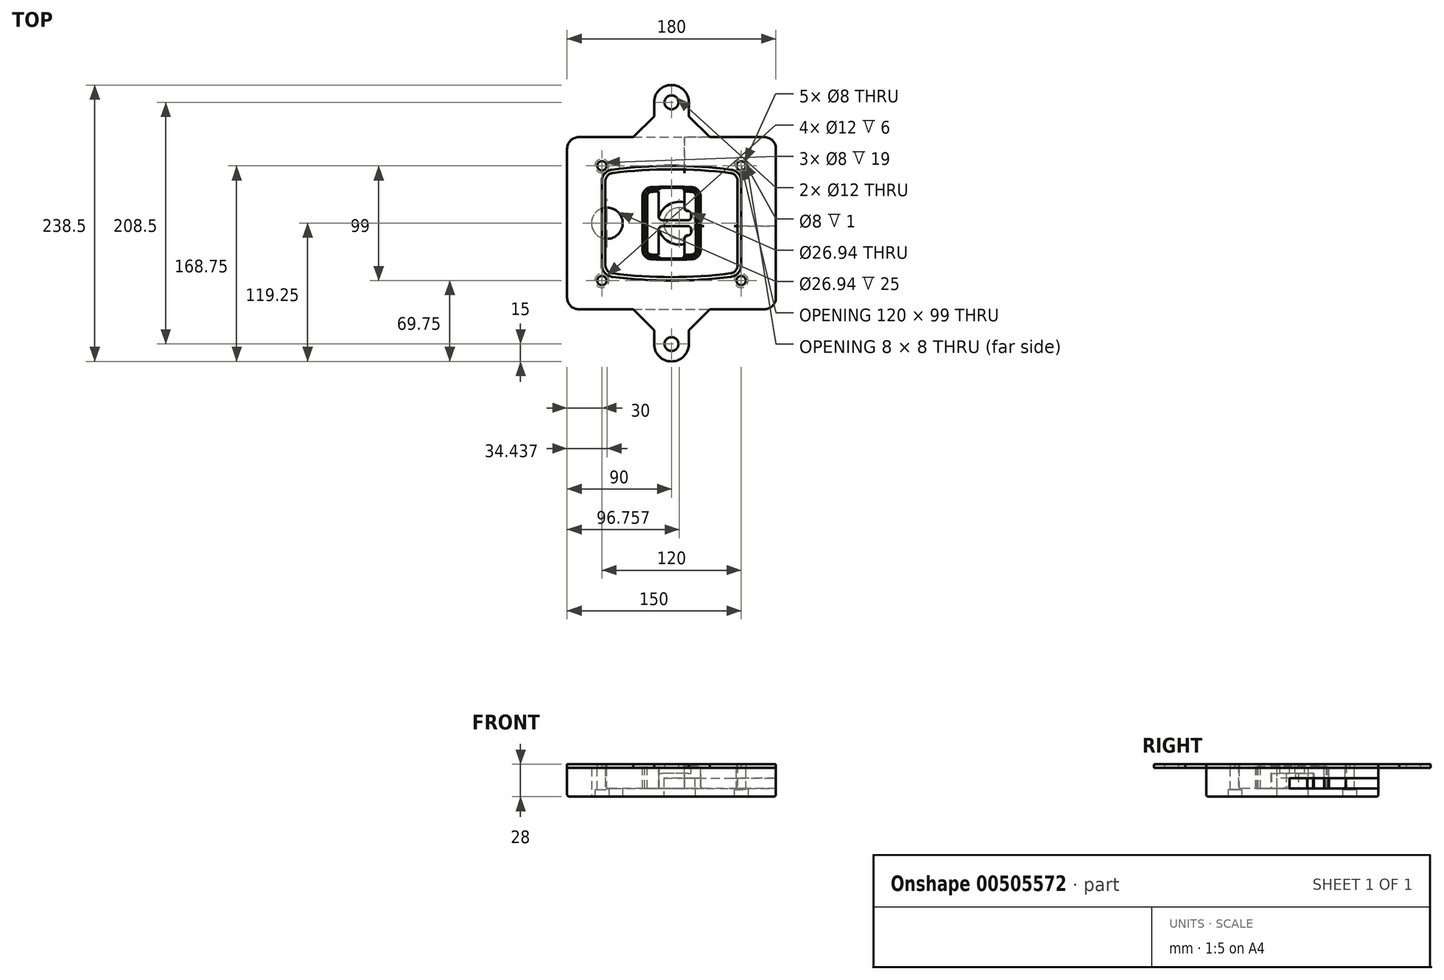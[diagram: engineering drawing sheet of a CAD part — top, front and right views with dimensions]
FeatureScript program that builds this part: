
annotation { "Feature Type Name" : "Feature", "Feature Type Description" : "" }
export const myFeature = defineFeature(function(context is Context, id is Id, definition is map)
    precondition{}
    {
        {
            var Q0;
            Q0=qCreatedBy(makeId("Top.planeOp"),FACE);
            var sketch = newSketch(context, id + "F0", { "sketchPlane" : qUnion([Q0])});
            skPoint(sketch, "E0.rect.middle", {"position": v(0, 0) * mm});
            skLineSegment(sketch, "E1.bottom", {"start": v(-80, -74.25) * mm, "end": v(80, -74.25) * mm});
            skLineSegment(sketch, "E1.top", {"start": v(-80, 74.25) * mm, "end": v(80, 74.25) * mm});
            skLineSegment(sketch, "E1.left", {"start": v(-90, -64.25) * mm, "end": v(-90, 64.25) * mm});
            skLineSegment(sketch, "E1.right", {"start": v(90, -64.25) * mm, "end": v(90, 64.25) * mm});
            skLineSegment(sketch, "E2", {"start": v(-90, 74.25) * mm, "end": v(90, -74.25) * mm, "construction": true});
            skLineSegment(sketch, "E3", {"start": v(90, 74.25) * mm, "end": v(-90, -74.25) * mm, "construction": true});
            skCircle(sketch, "E4", {"center": v(-60, 49.5) * mm, "radius": 4 * mm});
            skCircle(sketch, "E5", {"center": v(60, 49.5) * mm, "radius": 4 * mm});
            skCircle(sketch, "E6", {"center": v(60, -49.5) * mm, "radius": 4 * mm});
            skCircle(sketch, "E7", {"center": v(-60, -49.5) * mm, "radius": 4 * mm});
            skLineSegment(sketch, "E8", {"start": v(-60, 49.5) * mm, "end": v(60, 49.5) * mm, "construction": true});
            skLineSegment(sketch, "E9", {"start": v(60, 49.5) * mm, "end": v(60, -49.5) * mm, "construction": true});
            skLineSegment(sketch, "E10", {"start": v(60, -49.5) * mm, "end": v(-60, -49.5) * mm, "construction": true});
            skLineSegment(sketch, "E11", {"start": v(-60, -49.5) * mm, "end": v(-60, 49.5) * mm, "construction": true});
            skLineSegment(sketch, "E12", {"start": v(-60, 36.3) * mm, "end": v(-60, -36.3) * mm});
            skLineSegment(sketch, "E13", {"start": v(60, 36.3) * mm, "end": v(60, -36.3) * mm});
            skArc(sketch, "E14", {"start": v(51.27, 46.22) * mm, "mid": v(0, 49.5) * mm, "end": v(-51.27, 46.22) * mm});
            skArc(sketch, "E15", {"start": v(-51.27, -46.22) * mm, "mid": v(0, -49.5) * mm, "end": v(51.27, -46.22) * mm});
            skLineSegment(sketch, "E16", {"start": v(-60, 0) * mm, "end": v(60, 0) * mm, "construction": true});
            skPoint(sketch, "E17.visualSharp", {"position": v(-60, -45) * mm});
            skArc(sketch, "E17.filletArc", {"start": v(-60, -36.3) * mm, "mid": v(-57.5, -42.9) * mm, "end": v(-51.27, -46.22) * mm});
            skPoint(sketch, "E18.visualSharp", {"position": v(-60, 45) * mm});
            skArc(sketch, "E18.filletArc", {"start": v(-51.27, 46.22) * mm, "mid": v(-57.5, 42.9) * mm, "end": v(-60, 36.3) * mm});
            skPoint(sketch, "E19.visualSharp", {"position": v(60, 45) * mm});
            skArc(sketch, "E19.filletArc", {"start": v(60, 36.3) * mm, "mid": v(57.5, 42.9) * mm, "end": v(51.27, 46.22) * mm});
            skPoint(sketch, "E20.visualSharp", {"position": v(60, -45) * mm});
            skArc(sketch, "E20.filletArc", {"start": v(51.27, -46.22) * mm, "mid": v(57.5, -42.9) * mm, "end": v(60, -36.3) * mm});
            skPoint(sketch, "E21.visualSharp", {"position": v(-90, 74.25) * mm});
            skArc(sketch, "E21.filletArc", {"start": v(-80, 74.25) * mm, "mid": v(-87.07, 71.32) * mm, "end": v(-90, 64.25) * mm});
            skPoint(sketch, "E22.visualSharp", {"position": v(90, 74.25) * mm});
            skArc(sketch, "E22.filletArc", {"start": v(90, 64.25) * mm, "mid": v(87.07, 71.32) * mm, "end": v(80, 74.25) * mm});
            skPoint(sketch, "E23.visualSharp", {"position": v(90, -74.25) * mm});
            skArc(sketch, "E23.filletArc", {"start": v(80, -74.25) * mm, "mid": v(87.07, -71.32) * mm, "end": v(90, -64.25) * mm});
            skPoint(sketch, "E24.visualSharp", {"position": v(-90, -74.25) * mm});
            skArc(sketch, "E24.filletArc", {"start": v(-90, -64.25) * mm, "mid": v(-87.07, -71.32) * mm, "end": v(-80, -74.25) * mm});
            skArc(sketch, "E25.0", {"start": v(57, 36.3) * mm, "mid": v(55.26, 40.92) * mm, "end": v(50.9, 43.24) * mm});
            skLineSegment(sketch, "E25.1", {"start": v(57, 36.3) * mm, "end": v(57, -36.3) * mm});
            skArc(sketch, "E25.2", {"start": v(50.9, -43.24) * mm, "mid": v(55.26, -40.92) * mm, "end": v(57, -36.3) * mm});
            skArc(sketch, "E25.3", {"start": v(-50.9, -43.24) * mm, "mid": v(0, -46.5) * mm, "end": v(50.9, -43.24) * mm});
            skArc(sketch, "E25.4", {"start": v(-57, -36.3) * mm, "mid": v(-55.26, -40.92) * mm, "end": v(-50.9, -43.24) * mm});
            skArc(sketch, "E25.5", {"start": v(50.9, 43.24) * mm, "mid": v(0, 46.5) * mm, "end": v(-50.9, 43.24) * mm});
            skLineSegment(sketch, "E25.6", {"start": v(-57, 36.3) * mm, "end": v(-57, -36.3) * mm});
            skArc(sketch, "E25.7", {"start": v(-50.9, 43.24) * mm, "mid": v(-55.26, 40.92) * mm, "end": v(-57, 36.3) * mm});
            skArc(sketch, "E26.0", {"start": v(-51.78, 50.19) * mm, "mid": v(-60.51, 45.55) * mm, "end": v(-64, 36.3) * mm});
            skArc(sketch, "E26.1", {"start": v(51.78, 50.19) * mm, "mid": v(0, 53.5) * mm, "end": v(-51.78, 50.19) * mm});
            skArc(sketch, "E26.2", {"start": v(64, 36.3) * mm, "mid": v(60.51, 45.55) * mm, "end": v(51.78, 50.19) * mm});
            skLineSegment(sketch, "E26.3", {"start": v(64, 36.3) * mm, "end": v(64, -36.3) * mm});
            skArc(sketch, "E26.4", {"start": v(51.78, -50.19) * mm, "mid": v(60.51, -45.55) * mm, "end": v(64, -36.3) * mm});
            skLineSegment(sketch, "E26.5", {"start": v(-64, 36.3) * mm, "end": v(-64, -36.3) * mm});
            skArc(sketch, "E26.6", {"start": v(-51.78, -50.19) * mm, "mid": v(0, -53.5) * mm, "end": v(51.78, -50.19) * mm});
            skArc(sketch, "E26.7", {"start": v(-64, -36.3) * mm, "mid": v(-60.51, -45.55) * mm, "end": v(-51.78, -50.19) * mm});
            skSolve(sketch);
        }
        {
            var Q0;
            Q0=makeQuery(id+"F0.imprint","IMPRINT",FACE,{"disambiguationData":[TD([[makeQuery(id+"F0.imprint","IMPRINT",EDGE,{"derivedFrom":sQuery(id+"F0.wireOp",EDGE,"E1.bottom")}),1.0]])]});
            var Q1;
            Q1=makeQuery(id+"F0.imprint","IMPRINT",FACE,{"disambiguationData":[TD([[makeQuery(id+"F0.imprint","IMPRINT",EDGE,{"derivedFrom":sQuery(id+"F0.wireOp",EDGE,"E12")}),1.0]])]});
            var Q2;
            Q2=makeQuery(id+"F0.imprint","IMPRINT",FACE,{"disambiguationData":[TD([[makeQuery(id+"F0.imprint","IMPRINT",EDGE,{"derivedFrom":sQuery(id+"F0.wireOp",EDGE,"E25.0")}),1.0]])]});
            var Q3;
            Q3=makeQuery(id+"F0.imprint","IMPRINT",FACE,{"disambiguationData":[TD([[makeQuery(id+"F0.imprint","IMPRINT",EDGE,{"derivedFrom":sQuery(id+"F0.wireOp",EDGE,"E12")}),-1.0]])]});
            extrude(context, id + "F1", {"entities" : qUnion([Q0, Q1, Q2, Q3]), "oppositeDirection" : true, "depth" : 25 * mm});
        }
        {
            var Q0;
            Q0=makeQuery(id+"F0.imprint","IMPRINT",FACE,{"disambiguationData":[TD([[makeQuery(id+"F0.imprint","IMPRINT",EDGE,{"derivedFrom":sQuery(id+"F0.wireOp",EDGE,"E12")}),1.0]])]});
            extrude(context, id + "F2", {"entities" : qUnion([Q0]), "operationType" : NewBodyOperationType.ADD, "depth" : 3 * mm});
        }
        {
            var Q0;
            Q0=makeQuery(id+"F0.imprint","IMPRINT",FACE,{"disambiguationData":[TD([[makeQuery(id+"F0.imprint","IMPRINT",EDGE,{"derivedFrom":sQuery(id+"F0.wireOp",EDGE,"E25.0")}),1.0]])]});
            extrude(context, id + "F3", {"entities" : qUnion([Q0]), "operationType" : NewBodyOperationType.REMOVE, "oppositeDirection" : true, "depth" : 18 * mm});
        }
        {
            var Q0;
            Q0=makeQuery(id+"F2.opExtrude","CAP_FACE",FACE,{"disambiguationData":[OSD([sQuery(id+"F0.wireOp",EDGE,"E12"),sQuery(id+"F0.wireOp",EDGE,"E13"),sQuery(id+"F0.wireOp",EDGE,"E14"),sQuery(id+"F0.wireOp",EDGE,"E15"),sQuery(id+"F0.wireOp",EDGE,"E17.filletArc"),sQuery(id+"F0.wireOp",EDGE,"E18.filletArc"),sQuery(id+"F0.wireOp",EDGE,"E19.filletArc"),sQuery(id+"F0.wireOp",EDGE,"E20.filletArc"),sQuery(id+"F0.wireOp",EDGE,"E25.0"),sQuery(id+"F0.wireOp",EDGE,"E25.1"),sQuery(id+"F0.wireOp",EDGE,"E25.2"),sQuery(id+"F0.wireOp",EDGE,"E25.3"),sQuery(id+"F0.wireOp",EDGE,"E25.4"),sQuery(id+"F0.wireOp",EDGE,"E25.5"),sQuery(id+"F0.wireOp",EDGE,"E25.6"),sQuery(id+"F0.wireOp",EDGE,"E25.7")])],"isStart":false});
            var sketch = newSketch(context, id + "F4", { "sketchPlane" : qUnion([Q0])});
            skArc(sketch, "E27.0", {"start": v(-17.36, -31.1) * mm, "mid": v(0, -31.5) * mm, "end": v(17.36, -31.1) * mm});
            skArc(sketch, "E28.0", {"start": v(17.36, 31.1) * mm, "mid": v(0, 31.5) * mm, "end": v(-17.36, 31.1) * mm});
            skLineSegment(sketch, "E29", {"start": v(-25, 23.12) * mm, "end": v(-25, -23.12) * mm});
            skLineSegment(sketch, "E30", {"start": v(25, 23.12) * mm, "end": v(25, -23.12) * mm});
            skLineSegment(sketch, "E31", {"start": v(-25, 30.69) * mm, "end": v(25, 30.69) * mm, "construction": true});
            skLineSegment(sketch, "E32", {"start": v(-25, -30.69) * mm, "end": v(25, -30.69) * mm, "construction": true});
            skPoint(sketch, "E33.visualSharp", {"position": v(-25, 30.69) * mm});
            skArc(sketch, "E33.filletArc", {"start": v(-17.36, 31.1) * mm, "mid": v(-22.78, 28.64) * mm, "end": v(-25, 23.12) * mm});
            skPoint(sketch, "E34.visualSharp", {"position": v(25, 30.69) * mm});
            skArc(sketch, "E34.filletArc", {"start": v(25, 23.12) * mm, "mid": v(22.78, 28.64) * mm, "end": v(17.36, 31.1) * mm});
            skPoint(sketch, "E35.visualSharp", {"position": v(25, -30.69) * mm});
            skArc(sketch, "E35.filletArc", {"start": v(17.36, -31.1) * mm, "mid": v(22.78, -28.64) * mm, "end": v(25, -23.12) * mm});
            skPoint(sketch, "E36.visualSharp", {"position": v(-25, -30.69) * mm});
            skArc(sketch, "E36.filletArc", {"start": v(-25, -23.12) * mm, "mid": v(-22.78, -28.64) * mm, "end": v(-17.36, -31.1) * mm});
            skArc(sketch, "E37.0", {"start": v(50.9, 43.24) * mm, "mid": v(0, 46.5) * mm, "end": v(-50.9, 43.24) * mm});
            skArc(sketch, "E37.1", {"start": v(-50.9, 43.24) * mm, "mid": v(-55.26, 40.92) * mm, "end": v(-57, 36.3) * mm});
            skLineSegment(sketch, "E37.2", {"start": v(-57, 36.3) * mm, "end": v(-57, -36.3) * mm});
            skArc(sketch, "E37.3", {"start": v(-57, -36.3) * mm, "mid": v(-55.26, -40.92) * mm, "end": v(-50.9, -43.24) * mm});
            skArc(sketch, "E37.4", {"start": v(-50.9, -43.24) * mm, "mid": v(0, -46.5) * mm, "end": v(50.9, -43.24) * mm});
            skArc(sketch, "E37.5", {"start": v(50.9, -43.24) * mm, "mid": v(55.26, -40.92) * mm, "end": v(57, -36.3) * mm});
            skLineSegment(sketch, "E37.6", {"start": v(57, 36.3) * mm, "end": v(57, -36.3) * mm});
            skArc(sketch, "E37.7", {"start": v(57, 36.3) * mm, "mid": v(55.26, 40.92) * mm, "end": v(50.9, 43.24) * mm});
            skLineSegment(sketch, "E38.0", {"start": v(23, 23.12) * mm, "end": v(23, -23.12) * mm});
            skArc(sketch, "E38.1", {"start": v(17.27, -29.1) * mm, "mid": v(21.34, -27.26) * mm, "end": v(23, -23.12) * mm});
            skArc(sketch, "E38.2", {"start": v(-17.27, -29.1) * mm, "mid": v(0, -29.5) * mm, "end": v(17.27, -29.1) * mm});
            skArc(sketch, "E38.3", {"start": v(-23, -23.12) * mm, "mid": v(-21.34, -27.26) * mm, "end": v(-17.27, -29.1) * mm});
            skLineSegment(sketch, "E38.4", {"start": v(-23, 23.12) * mm, "end": v(-23, -23.12) * mm});
            skArc(sketch, "E38.5", {"start": v(23, 23.12) * mm, "mid": v(21.34, 27.26) * mm, "end": v(17.27, 29.1) * mm});
            skArc(sketch, "E38.6", {"start": v(-17.27, 29.1) * mm, "mid": v(-21.34, 27.26) * mm, "end": v(-23, 23.12) * mm});
            skArc(sketch, "E38.7", {"start": v(17.27, 29.1) * mm, "mid": v(0, 29.5) * mm, "end": v(-17.27, 29.1) * mm});
            skArc(sketch, "E39.0", {"start": v(21, 23.12) * mm, "mid": v(19.9, 25.88) * mm, "end": v(17.18, 27.11) * mm});
            skLineSegment(sketch, "E39.1", {"start": v(21, 23.12) * mm, "end": v(21, -23.12) * mm});
            skArc(sketch, "E39.2", {"start": v(17.18, -27.11) * mm, "mid": v(19.9, -25.88) * mm, "end": v(21, -23.12) * mm});
            skArc(sketch, "E39.3", {"start": v(-17.18, -27.11) * mm, "mid": v(0, -27.5) * mm, "end": v(17.18, -27.11) * mm});
            skArc(sketch, "E39.4", {"start": v(-21, -23.12) * mm, "mid": v(-19.9, -25.88) * mm, "end": v(-17.18, -27.11) * mm});
            skArc(sketch, "E39.5", {"start": v(17.18, 27.11) * mm, "mid": v(0, 27.5) * mm, "end": v(-17.18, 27.11) * mm});
            skLineSegment(sketch, "E39.6", {"start": v(-21, 23.12) * mm, "end": v(-21, -23.12) * mm});
            skArc(sketch, "E39.7", {"start": v(-17.18, 27.11) * mm, "mid": v(-19.9, 25.88) * mm, "end": v(-21, 23.12) * mm});
            skLineSegment(sketch, "E40", {"start": v(-25, 0) * mm, "end": v(25, 0) * mm, "construction": true});
            skLineSegment(sketch, "E41", {"start": v(-11, 5.5) * mm, "end": v(-11, 27.5) * mm});
            skLineSegment(sketch, "E42", {"start": v(-8, 30.5) * mm, "end": v(8, 30.5) * mm});
            skLineSegment(sketch, "E43", {"start": v(11, 27.5) * mm, "end": v(11, 13.5) * mm});
            skLineSegment(sketch, "E44", {"start": v(14, 10.5) * mm, "end": v(14, 10.5) * mm});
            skLineSegment(sketch, "E45", {"start": v(17, 7.5) * mm, "end": v(17, 5.5) * mm});
            skLineSegment(sketch, "E46", {"start": v(14, 2.5) * mm, "end": v(-8, 2.5) * mm});
            skPoint(sketch, "E47.visualSharp", {"position": v(-11, 30.5) * mm});
            skArc(sketch, "E47.filletArc", {"start": v(-8, 30.5) * mm, "mid": v(-10.12, 29.62) * mm, "end": v(-11, 27.5) * mm});
            skPoint(sketch, "E48.visualSharp", {"position": v(11, 30.5) * mm});
            skArc(sketch, "E48.filletArc", {"start": v(11, 27.5) * mm, "mid": v(10.12, 29.62) * mm, "end": v(8, 30.5) * mm});
            skPoint(sketch, "E49.visualSharp", {"position": v(11, 10.5) * mm});
            skArc(sketch, "E49.filletArc", {"start": v(11, 13.5) * mm, "mid": v(11.88, 11.38) * mm, "end": v(14, 10.5) * mm});
            skPoint(sketch, "E50.visualSharp", {"position": v(17, 10.5) * mm});
            skArc(sketch, "E50.filletArc", {"start": v(17, 7.5) * mm, "mid": v(16.12, 9.62) * mm, "end": v(14, 10.5) * mm});
            skPoint(sketch, "E51.visualSharp", {"position": v(17, 2.5) * mm});
            skArc(sketch, "E51.filletArc", {"start": v(14, 2.5) * mm, "mid": v(16.12, 3.38) * mm, "end": v(17, 5.5) * mm});
            skPoint(sketch, "E52.visualSharp", {"position": v(-11, 2.5) * mm});
            skArc(sketch, "E52.filletArc", {"start": v(-11, 5.5) * mm, "mid": v(-10.12, 3.38) * mm, "end": v(-8, 2.5) * mm});
            skLineSegment(sketch, "E53.0.MirrorCS", {"start": v(14, -2.5) * mm, "end": v(-8, -2.5) * mm});
            skArc(sketch, "E54.0.MirrorCS", {"start": v(-11, -5.5) * mm, "mid": v(-10.12, -3.38) * mm, "end": v(-8, -2.5) * mm});
            skLineSegment(sketch, "E55.0.MirrorCS", {"start": v(-11, -5.5) * mm, "end": v(-11, -27.5) * mm});
            skArc(sketch, "E56.0.MirrorCS", {"start": v(-8, -30.5) * mm, "mid": v(-10.12, -29.62) * mm, "end": v(-11, -27.5) * mm});
            skLineSegment(sketch, "E57.0.MirrorCS", {"start": v(-8, -30.5) * mm, "end": v(8, -30.5) * mm});
            skArc(sketch, "E58.0.MirrorCS", {"start": v(11, -27.5) * mm, "mid": v(10.12, -29.62) * mm, "end": v(8, -30.5) * mm});
            skLineSegment(sketch, "E59.0.MirrorCS", {"start": v(11, -27.5) * mm, "end": v(11, -13.5) * mm});
            skArc(sketch, "E60.0.MirrorCS", {"start": v(11, -13.5) * mm, "mid": v(11.88, -11.38) * mm, "end": v(14, -10.5) * mm});
            skArc(sketch, "E61.0.MirrorCS", {"start": v(17, -7.5) * mm, "mid": v(16.12, -9.62) * mm, "end": v(14, -10.5) * mm});
            skLineSegment(sketch, "E62.0.MirrorCS", {"start": v(17, -7.5) * mm, "end": v(17, -5.5) * mm});
            skArc(sketch, "E63.0.MirrorCS", {"start": v(14, -2.5) * mm, "mid": v(16.12, -3.38) * mm, "end": v(17, -5.5) * mm});
            skSolve(sketch);
        }
        {
            var Q0;
            Q0=makeQuery(id+"F4.imprint","IMPRINT",FACE,{"disambiguationData":[TD([[makeQuery(id+"F4.imprint","IMPRINT",EDGE,{"derivedFrom":sQuery(id+"F4.wireOp",EDGE,"E27.0")}),1.0]])]});
            var Q1;
            Q1=makeQuery(id+"F4.imprint","IMPRINT",FACE,{"disambiguationData":[TD([[makeQuery(id+"F4.imprint","IMPRINT",EDGE,{"derivedFrom":sQuery(id+"F4.wireOp",EDGE,"E38.0")}),-1.0]])]});
            var Q2;
            Q2=makeQuery(id+"F4.imprint","IMPRINT",FACE,{"disambiguationData":[TD([[makeQuery(id+"F4.imprint","IMPRINT",EDGE,{"derivedFrom":sQuery(id+"F4.wireOp",EDGE,"E39.0")}),1.0]])]});
            extrude(context, id + "F5", {"entities" : qUnion([Q0, Q1, Q2]), "operationType" : NewBodyOperationType.ADD, "endBound" : BoundingType.UP_TO_NEXT, "oppositeDirection" : true, "depth" : 25 * mm});
        }
        {
            var Q0;
            Q0=makeQuery(id+"F4.imprint","IMPRINT",FACE,{"disambiguationData":[TD([[makeQuery(id+"F4.imprint","IMPRINT",EDGE,{"derivedFrom":sQuery(id+"F4.wireOp",EDGE,"E38.0")}),-1.0]])]});
            extrude(context, id + "F6", {"entities" : qUnion([Q0]), "operationType" : NewBodyOperationType.REMOVE, "oppositeDirection" : true, "depth" : 2 * mm});
        }
        {
            var Q0;
            Q0=makeQuery(id+"F1.opExtrude","CAP_FACE",FACE,{"disambiguationData":[OSD([sQuery(id+"F0.wireOp",EDGE,"E1.bottom"),sQuery(id+"F0.wireOp",EDGE,"E1.top"),sQuery(id+"F0.wireOp",EDGE,"E1.left"),sQuery(id+"F0.wireOp",EDGE,"E1.right"),sQuery(id+"F0.wireOp",EDGE,"E4"),sQuery(id+"F0.wireOp",EDGE,"E5"),sQuery(id+"F0.wireOp",EDGE,"E6"),sQuery(id+"F0.wireOp",EDGE,"E7"),sQuery(id+"F0.wireOp",EDGE,"E21.filletArc"),sQuery(id+"F0.wireOp",EDGE,"E22.filletArc"),sQuery(id+"F0.wireOp",EDGE,"E23.filletArc"),sQuery(id+"F0.wireOp",EDGE,"E24.filletArc")])],"isStart":false});
            var sketch = newSketch(context, id + "F7", { "sketchPlane" : qUnion([Q0])});
            skCircle(sketch, "E64", {"center": v(6.76, 0) * mm, "radius": 13.47 * mm});
            skCircle(sketch, "E65", {"center": v(-55.56, 0) * mm, "radius": 13.47 * mm});
            skLineSegment(sketch, "E66", {"start": v(90, 0) * mm, "end": v(-90, 0) * mm});
            skCircle(sketch, "E67", {"center": v(6.76, 0) * mm, "radius": 18.47 * mm});
            skCircle(sketch, "E68", {"center": v(60, -49.5) * mm, "radius": 6 * mm});
            skCircle(sketch, "E69", {"center": v(-60, -49.5) * mm, "radius": 6 * mm});
            skCircle(sketch, "E70", {"center": v(-60, 49.5) * mm, "radius": 6 * mm});
            skCircle(sketch, "E71", {"center": v(60, 49.5) * mm, "radius": 6 * mm});
            skSolve(sketch);
        }
        {
            var Q0;
            {var subQ1=sQuery(id+"F7.wireOp",EDGE,"E66");var subQ4=sQuery(id+"F7.wireOp",EDGE,"E64");var subQ6=makeQuery(id+"F7.imprint","INTERSECT",VERTEX,{"disambiguationData":[OD(0.0)],"derivedFrom":[subQ4,subQ1]});Q0=makeQuery(id+"F7.imprint","IMPRINT",FACE,{"disambiguationData":[TD([[makeQuery(id+"F7.imprint","IMPRINT",EDGE,{"disambiguationData":[TD([[subQ6,-1.0]])],"derivedFrom":subQ4}),-1.0]])]});}
            var Q1;
            {var subQ0=sQuery(id+"F7.wireOp",EDGE,"E66");var subQ1=sQuery(id+"F7.wireOp",EDGE,"E64");var subQ3=makeQuery(id+"F7.imprint","INTERSECT",VERTEX,{"disambiguationData":[OD(0.0)],"derivedFrom":[subQ1,subQ0]});Q1=makeQuery(id+"F7.imprint","IMPRINT",FACE,{"disambiguationData":[TD([[makeQuery(id+"F7.imprint","IMPRINT",EDGE,{"disambiguationData":[TD([[subQ3,-1.0]])],"derivedFrom":subQ1}),1.0]])]});}
            var Q2;
            {var subQ0=sQuery(id+"F7.wireOp",EDGE,"E66");var subQ1=sQuery(id+"F7.wireOp",EDGE,"E64");var subQ3=makeQuery(id+"F7.imprint","INTERSECT",VERTEX,{"disambiguationData":[OD(0.0)],"derivedFrom":[subQ1,subQ0]});Q2=makeQuery(id+"F7.imprint","IMPRINT",FACE,{"disambiguationData":[TD([[makeQuery(id+"F7.imprint","IMPRINT",EDGE,{"disambiguationData":[TD([[subQ3,1.0]])],"derivedFrom":subQ1}),1.0]])]});}
            var Q3;
            {var subQ1=sQuery(id+"F7.wireOp",EDGE,"E66");var subQ4=sQuery(id+"F7.wireOp",EDGE,"E64");var subQ6=makeQuery(id+"F7.imprint","INTERSECT",VERTEX,{"disambiguationData":[OD(0.0)],"derivedFrom":[subQ4,subQ1]});Q3=makeQuery(id+"F7.imprint","IMPRINT",FACE,{"disambiguationData":[TD([[makeQuery(id+"F7.imprint","IMPRINT",EDGE,{"disambiguationData":[TD([[subQ6,1.0]])],"derivedFrom":subQ4}),-1.0]])]});}
            extrude(context, id + "F8", {"entities" : qUnion([Q0, Q1, Q2, Q3]), "operationType" : NewBodyOperationType.ADD, "oppositeDirection" : true, "depth" : 20 * mm});
        }
        {
            var Q0;
            {var subQ0=sQuery(id+"F7.wireOp",EDGE,"E66");var subQ1=sQuery(id+"F7.wireOp",EDGE,"E64");var subQ3=makeQuery(id+"F7.imprint","INTERSECT",VERTEX,{"disambiguationData":[OD(0.0)],"derivedFrom":[subQ1,subQ0]});Q0=makeQuery(id+"F7.imprint","IMPRINT",FACE,{"disambiguationData":[TD([[makeQuery(id+"F7.imprint","IMPRINT",EDGE,{"disambiguationData":[TD([[subQ3,-1.0]])],"derivedFrom":subQ1}),1.0]])]});}
            var Q1;
            {var subQ0=sQuery(id+"F7.wireOp",EDGE,"E66");var subQ1=sQuery(id+"F7.wireOp",EDGE,"E64");var subQ3=makeQuery(id+"F7.imprint","INTERSECT",VERTEX,{"disambiguationData":[OD(0.0)],"derivedFrom":[subQ1,subQ0]});Q1=makeQuery(id+"F7.imprint","IMPRINT",FACE,{"disambiguationData":[TD([[makeQuery(id+"F7.imprint","IMPRINT",EDGE,{"disambiguationData":[TD([[subQ3,1.0]])],"derivedFrom":subQ1}),1.0]])]});}
            extrude(context, id + "F9", {"entities" : qUnion([Q0, Q1]), "operationType" : NewBodyOperationType.REMOVE, "oppositeDirection" : true, "depth" : 16 * mm});
        }
        {
            var Q0;
            {var subQ0=sQuery(id+"F7.wireOp",EDGE,"E66");var subQ1=sQuery(id+"F7.wireOp",EDGE,"E65");var subQ3=makeQuery(id+"F7.imprint","INTERSECT",VERTEX,{"disambiguationData":[OD(0.0)],"derivedFrom":[subQ1,subQ0]});Q0=makeQuery(id+"F7.imprint","IMPRINT",FACE,{"disambiguationData":[TD([[makeQuery(id+"F7.imprint","IMPRINT",EDGE,{"disambiguationData":[TD([[subQ3,-1.0]])],"derivedFrom":subQ1}),1.0]])]});}
            var Q1;
            {var subQ0=sQuery(id+"F7.wireOp",EDGE,"E66");var subQ1=sQuery(id+"F7.wireOp",EDGE,"E65");var subQ3=makeQuery(id+"F7.imprint","INTERSECT",VERTEX,{"disambiguationData":[OD(0.0)],"derivedFrom":[subQ1,subQ0]});Q1=makeQuery(id+"F7.imprint","IMPRINT",FACE,{"disambiguationData":[TD([[makeQuery(id+"F7.imprint","IMPRINT",EDGE,{"disambiguationData":[TD([[subQ3,1.0]])],"derivedFrom":subQ1}),1.0]])]});}
            extrude(context, id + "F10", {"entities" : qUnion([Q0, Q1]), "operationType" : NewBodyOperationType.REMOVE, "oppositeDirection" : true, "depth" : 25 * mm});
        }
        {
            var Q0;
            Q0=makeQuery(id+"F7.imprint","IMPRINT",FACE,{"disambiguationData":[TD([[makeQuery(id+"F7.imprint","IMPRINT",EDGE,{"derivedFrom":sQuery(id+"F7.wireOp",EDGE,"E68")}),1.0]])]});
            var Q1;
            Q1=makeQuery(id+"F7.imprint","IMPRINT",FACE,{"disambiguationData":[TD([[makeQuery(id+"F7.imprint","IMPRINT",EDGE,{"derivedFrom":makeQuery(id+"F1.opExtrude","CAP_EDGE",EDGE,{"disambiguationData":[OSD([sQuery(id+"F0.wireOp",EDGE,"E5")])],"isStart":false})}),-1.0]])]});
            var Q2;
            Q2=makeQuery(id+"F7.imprint","IMPRINT",FACE,{"disambiguationData":[TD([[makeQuery(id+"F7.imprint","IMPRINT",EDGE,{"derivedFrom":sQuery(id+"F7.wireOp",EDGE,"E69")}),1.0]])]});
            var Q3;
            Q3=makeQuery(id+"F7.imprint","IMPRINT",FACE,{"disambiguationData":[TD([[makeQuery(id+"F7.imprint","IMPRINT",EDGE,{"derivedFrom":makeQuery(id+"F1.opExtrude","CAP_EDGE",EDGE,{"disambiguationData":[OSD([sQuery(id+"F0.wireOp",EDGE,"E4")])],"isStart":false})}),-1.0]])]});
            var Q4;
            Q4=makeQuery(id+"F7.imprint","IMPRINT",FACE,{"disambiguationData":[TD([[makeQuery(id+"F7.imprint","IMPRINT",EDGE,{"derivedFrom":sQuery(id+"F7.wireOp",EDGE,"E70")}),1.0]])]});
            var Q5;
            Q5=makeQuery(id+"F7.imprint","IMPRINT",FACE,{"disambiguationData":[TD([[makeQuery(id+"F7.imprint","IMPRINT",EDGE,{"derivedFrom":makeQuery(id+"F1.opExtrude","CAP_EDGE",EDGE,{"disambiguationData":[OSD([sQuery(id+"F0.wireOp",EDGE,"E7")])],"isStart":false})}),-1.0]])]});
            var Q6;
            Q6=makeQuery(id+"F7.imprint","IMPRINT",FACE,{"disambiguationData":[TD([[makeQuery(id+"F7.imprint","IMPRINT",EDGE,{"derivedFrom":sQuery(id+"F7.wireOp",EDGE,"E71")}),1.0]])]});
            var Q7;
            Q7=makeQuery(id+"F7.imprint","IMPRINT",FACE,{"disambiguationData":[TD([[makeQuery(id+"F7.imprint","IMPRINT",EDGE,{"derivedFrom":makeQuery(id+"F1.opExtrude","CAP_EDGE",EDGE,{"disambiguationData":[OSD([sQuery(id+"F0.wireOp",EDGE,"E6")])],"isStart":false})}),-1.0]])]});
            extrude(context, id + "F11", {"entities" : qUnion([Q0, Q1, Q2, Q3, Q4, Q5, Q6, Q7]), "operationType" : NewBodyOperationType.REMOVE, "oppositeDirection" : true, "depth" : 6 * mm});
        }
        {
            var Q0;
            Q0=makeQuery(id+"F9.boolean.opBoolean","COPY",FACE,{"derivedFrom":makeQuery(id+"F9.opExtrude","CAP_FACE",FACE,{"disambiguationData":[OSD([sQuery(id+"F7.wireOp",EDGE,"E64")])],"isStart":false})});
            var sketch = newSketch(context, id + "F12", { "sketchPlane" : qUnion([Q0])});
            skArc(sketch, "E72.0", {"start": v(11, -88.19) * mm, "mid": v(97.1, -83.6) * mm, "end": v(92.5, 2.5) * mm});
            skLineSegment(sketch, "E72.1", {"start": v(11, -17.97) * mm, "end": v(11, -17.97) * mm});
            skLineSegment(sketch, "E73", {"start": v(92.5, -105.13) * mm, "end": v(102.3, -105.13) * mm});
            skLineSegment(sketch, "E74.0", {"start": v(92.5, 2.5) * mm, "end": v(14, 2.5) * mm});
            skArc(sketch, "E74.1", {"start": v(14, 2.5) * mm, "mid": v(16.12, 3.38) * mm, "end": v(17, 5.5) * mm});
            skLineSegment(sketch, "E74.2", {"start": v(17, 7.5) * mm, "end": v(17, 5.5) * mm});
            skArc(sketch, "E74.3", {"start": v(17, 7.5) * mm, "mid": v(16.12, 9.62) * mm, "end": v(14, 10.5) * mm});
            skArc(sketch, "E74.4", {"start": v(11, 13.5) * mm, "mid": v(11.88, 11.38) * mm, "end": v(14, 10.5) * mm});
            skLineSegment(sketch, "E74.5", {"start": v(11, 13.5) * mm, "end": v(11, -88.19) * mm});
            skLineSegment(sketch, "E74.7", {"start": v(92.5, -2.5) * mm, "end": v(14, -2.5) * mm});
            skArc(sketch, "E74.8", {"start": v(14, -2.5) * mm, "mid": v(16.12, -3.38) * mm, "end": v(17, -5.5) * mm});
            skLineSegment(sketch, "E74.9", {"start": v(17, -7.5) * mm, "end": v(17, -5.5) * mm});
            skArc(sketch, "E74.10", {"start": v(17, -7.5) * mm, "mid": v(16.12, -9.62) * mm, "end": v(14, -10.5) * mm});
            skArc(sketch, "E74.11", {"start": v(11, -13.5) * mm, "mid": v(11.88, -11.38) * mm, "end": v(14, -10.5) * mm});
            skLineSegment(sketch, "E74.12", {"start": v(11, -17.97) * mm, "end": v(11, -13.5) * mm});
            skPoint(sketch, "E75.orphan", {"position": v(11, -130.13) * mm});
            skPoint(sketch, "E76.orphan", {"position": v(-8, -2.5) * mm});
            skPoint(sketch, "E77.orphan", {"position": v(-8, 2.5) * mm});
            skPoint(sketch, "E78.orphan", {"position": v(11, -75.13) * mm});
            skSolve(sketch);
        }
        {
            var Q0;
            {var subQ7=sQuery(id+"F12.wireOp",EDGE,"E72.0");var subQ14=sQuery(id+"F12.wireOp",EDGE,"E72.1");var subQ16=sQuery(id+"F12.wireOp",EDGE,"E74.1");var subQ18=sQuery(id+"F12.wireOp",EDGE,"E74.8");Q0=qUnion([makeQuery(id+"F12.imprint","IMPRINT",FACE,{"disambiguationData":[TD([[makeQuery(id+"F12.imprint","IMPRINT",EDGE,{"derivedFrom":subQ7}),1.0]])]}),makeQuery(id+"F12.imprint","IMPRINT",FACE,{"disambiguationData":[TD([[makeQuery(id+"F12.imprint","IMPRINT",EDGE,{"derivedFrom":subQ14}),1.0]])]}),makeQuery(id+"F12.imprint","IMPRINT",FACE,{"disambiguationData":[TD([[makeQuery(id+"F12.imprint","IMPRINT",EDGE,{"derivedFrom":subQ16}),1.0]])]}),makeQuery(id+"F12.imprint","IMPRINT",FACE,{"disambiguationData":[TD([[makeQuery(id+"F12.imprint","IMPRINT",EDGE,{"derivedFrom":subQ18}),-1.0]])]})]);}
            var Q1;
            Q1=makeQuery(id+"F5.boolean.opBoolean","SPLIT",FACE,{"disambiguationData":[TD([makeQuery(id+"F5.opExtrude","SWEPT_FACE",FACE,{"disambiguationData":[OSD([sQuery(id+"F4.wireOp",EDGE,"E41")])]})])],"derivedFrom":makeQuery(id+"F3.boolean.opBoolean","COPY",FACE,{"derivedFrom":makeQuery(id+"F3.opExtrude","CAP_FACE",FACE,{"disambiguationData":[OSD([sQuery(id+"F0.wireOp",EDGE,"E25.0"),sQuery(id+"F0.wireOp",EDGE,"E25.1"),sQuery(id+"F0.wireOp",EDGE,"E25.2"),sQuery(id+"F0.wireOp",EDGE,"E25.3"),sQuery(id+"F0.wireOp",EDGE,"E25.4"),sQuery(id+"F0.wireOp",EDGE,"E25.5"),sQuery(id+"F0.wireOp",EDGE,"E25.6"),sQuery(id+"F0.wireOp",EDGE,"E25.7")])],"isStart":false})})});
            extrude(context, id + "F13", {"entities" : qUnion([Q0]), "operationType" : NewBodyOperationType.REMOVE, "endBound" : BoundingType.UP_TO_SURFACE, "endBoundEntityFace" : qUnion([Q1]), "depth" : 25 * mm});
        }
        {
            var Q0;
            Q0=makeQuery(id+"F3.boolean.opBoolean","COPY",EDGE,{"derivedFrom":makeQuery(id+"F3.opExtrude","CAP_EDGE",EDGE,{"disambiguationData":[OSD([sQuery(id+"F0.wireOp",EDGE,"E25.6")])],"isStart":false})});
            var Q1;
            Q1=makeQuery(id+"F8.boolean.opBoolean","INTERSECT",EDGE,{"derivedFrom":[makeQuery(id+"F5.opExtrude","SWEPT_FACE",FACE,{"disambiguationData":[OSD([sQuery(id+"F4.wireOp",EDGE,"E30")])]}),makeQuery(id+"F8.opExtrude","CAP_FACE",FACE,{"disambiguationData":[OSD([sQuery(id+"F7.wireOp",EDGE,"E67")])],"isStart":false})]});
            var Q2;
            Q2=makeQuery(id+"F8.boolean.opBoolean","INTERSECT",EDGE,{"disambiguationData":[OD(1.0)],"derivedFrom":[makeQuery(id+"F5.opExtrude","SWEPT_FACE",FACE,{"disambiguationData":[OSD([sQuery(id+"F4.wireOp",EDGE,"E30")])]}),makeQuery(id+"F8.opExtrude","SWEPT_FACE",FACE,{"disambiguationData":[OSD([sQuery(id+"F7.wireOp",EDGE,"E67")])]})]});
            var Q3;
            {var subQ0=makeQuery(id+"F3.boolean.opBoolean","COPY",FACE,{"derivedFrom":makeQuery(id+"F3.opExtrude","CAP_FACE",FACE,{"disambiguationData":[OSD([sQuery(id+"F0.wireOp",EDGE,"E25.0"),sQuery(id+"F0.wireOp",EDGE,"E25.1"),sQuery(id+"F0.wireOp",EDGE,"E25.2"),sQuery(id+"F0.wireOp",EDGE,"E25.3"),sQuery(id+"F0.wireOp",EDGE,"E25.4"),sQuery(id+"F0.wireOp",EDGE,"E25.5"),sQuery(id+"F0.wireOp",EDGE,"E25.6"),sQuery(id+"F0.wireOp",EDGE,"E25.7")])],"isStart":false})});var subQ1=sQuery(id+"F4.wireOp",EDGE,"E30");Q3=makeQuery(id+"F8.boolean.opBoolean","SPLIT",EDGE,{"disambiguationData":[TD([makeQuery(id+"F5.opExtrude","SWEPT_FACE",FACE,{"disambiguationData":[OSD([sQuery(id+"F4.wireOp",EDGE,"E35.filletArc")])]})])],"derivedFrom":makeQuery(id+"F5.opExtrude","TWEAK_EDGE",EDGE,{"derivedFrom":[subQ0,makeQuery(id+"F4.imprint","IMPRINT",EDGE,{"derivedFrom":subQ1})]})});}
            var Q4;
            {var subQ0=sQuery(id+"F0.wireOp",EDGE,"E25.0");var subQ1=sQuery(id+"F0.wireOp",EDGE,"E25.1");var subQ2=sQuery(id+"F0.wireOp",EDGE,"E25.2");var subQ3=sQuery(id+"F0.wireOp",EDGE,"E25.3");var subQ4=sQuery(id+"F0.wireOp",EDGE,"E25.4");var subQ5=sQuery(id+"F0.wireOp",EDGE,"E25.5");var subQ6=sQuery(id+"F0.wireOp",EDGE,"E25.6");var subQ7=sQuery(id+"F0.wireOp",EDGE,"E25.7");Q4=makeQuery(id+"F8.boolean.opBoolean","INTERSECT",EDGE,{"derivedFrom":[makeQuery(id+"F5.boolean.opBoolean","SPLIT",FACE,{"disambiguationData":[TD([makeQuery(id+"F2.opExtrude","SWEPT_FACE",FACE,{"disambiguationData":[OSD([subQ0])]})])],"derivedFrom":makeQuery(id+"F3.boolean.opBoolean","COPY",FACE,{"derivedFrom":makeQuery(id+"F3.opExtrude","CAP_FACE",FACE,{"disambiguationData":[OSD([subQ0,subQ1,subQ2,subQ3,subQ4,subQ5,subQ6,subQ7])],"isStart":false})})}),makeQuery(id+"F8.opExtrude","SWEPT_FACE",FACE,{"disambiguationData":[OSD([sQuery(id+"F7.wireOp",EDGE,"E67")])]})]});}
            var Q5;
            Q5=makeQuery(id+"F8.boolean.opBoolean","INTERSECT",EDGE,{"disambiguationData":[OD(0.0)],"derivedFrom":[makeQuery(id+"F5.opExtrude","SWEPT_FACE",FACE,{"disambiguationData":[OSD([sQuery(id+"F4.wireOp",EDGE,"E30")])]}),makeQuery(id+"F8.opExtrude","SWEPT_FACE",FACE,{"disambiguationData":[OSD([sQuery(id+"F7.wireOp",EDGE,"E67")])]})]});
            fillet(context, id + "F14", {"entities" : qUnion([Q0, Q1, Q2, Q3, Q4, Q5]), "radius" : 3 * mm, "tangentPropagation" : true, "allowEdgeOverflow" : false});
        }
        {
            var Q0;
            Q0=makeQuery(id+"F1.opExtrude","CAP_EDGE",EDGE,{"disambiguationData":[OSD([sQuery(id+"F0.wireOp",EDGE,"E1.bottom")])],"isStart":false});
            fillet(context, id + "F15", {"entities" : qUnion([Q0]), "radius" : 2 * mm, "tangentPropagation" : true, "allowEdgeOverflow" : false});
        }
        {
            var Q0;
            {var subQ0=sQuery(id+"F0.wireOp",EDGE,"E21.filletArc");var subQ1=sQuery(id+"F0.wireOp",EDGE,"E7");var subQ2=sQuery(id+"F0.wireOp",EDGE,"E6");var subQ3=sQuery(id+"F0.wireOp",EDGE,"E5");var subQ4=sQuery(id+"F0.wireOp",EDGE,"E4");var subQ5=sQuery(id+"F0.wireOp",EDGE,"E22.filletArc");var subQ6=sQuery(id+"F0.wireOp",EDGE,"E1.bottom");var subQ7=sQuery(id+"F0.wireOp",EDGE,"E1.right");var subQ8=sQuery(id+"F0.wireOp",EDGE,"E1.top");var subQ9=sQuery(id+"F0.wireOp",EDGE,"E1.left");var subQ10=sQuery(id+"F0.wireOp",EDGE,"E23.filletArc");var subQ11=sQuery(id+"F0.wireOp",EDGE,"E24.filletArc");Q0=makeQuery(id+"F2.boolean.opBoolean","SPLIT",FACE,{"disambiguationData":[TD([makeQuery(id+"F1.opExtrude","SWEPT_FACE",FACE,{"disambiguationData":[OSD([subQ6])]})])],"derivedFrom":makeQuery(id+"F1.opExtrude","CAP_FACE",FACE,{"disambiguationData":[OSD([subQ6,subQ8,subQ9,subQ7,subQ4,subQ3,subQ2,subQ1,subQ0,subQ5,subQ10,subQ11])],"isStart":true})});}
            var sketch = newSketch(context, id + "F16", { "sketchPlane" : qUnion([Q0])});
            skSolve(sketch);
        }
        {
            var Q0;
            Q0=makeQuery(id+"F16.imprint","IMPRINT",FACE,{"disambiguationData":[TD([[makeQuery(id+"F16.imprint","IMPRINT",EDGE,{"derivedFrom":makeQuery(id+"F1.opExtrude","CAP_EDGE",EDGE,{"disambiguationData":[OSD([sQuery(id+"F0.wireOp",EDGE,"E1.bottom")])],"isStart":true})}),1.0]])]});
            var sketch = newSketch(context, id + "F17", { "sketchPlane" : qUnion([Q0])});
            skCircle(sketch, "E79", {"center": v(0, 104.25) * mm, "radius": 6 * mm});
            skLineSegment(sketch, "E80.0", {"start": v(-80, 74.25) * mm, "end": v(80, 74.25) * mm});
            skLineSegment(sketch, "E81", {"start": v(0, 74.25) * mm, "end": v(0, 104.25) * mm, "construction": true});
            skLineSegment(sketch, "E82", {"start": v(-33, 74.25) * mm, "end": v(-15, 92.25) * mm});
            skLineSegment(sketch, "E83", {"start": v(15, 92.25) * mm, "end": v(33, 74.25) * mm});
            skLineSegment(sketch, "E84", {"start": v(-15, 92.25) * mm, "end": v(-15, 104.25) * mm});
            skLineSegment(sketch, "E85", {"start": v(15, 92.25) * mm, "end": v(15, 104.25) * mm});
            skArc(sketch, "E86", {"start": v(15, 104.25) * mm, "mid": v(0, 119.25) * mm, "end": v(-15, 104.25) * mm});
            skLineSegment(sketch, "E87", {"start": v(-75.58, 0) * mm, "end": v(74.81, 0) * mm, "construction": true});
            skLineSegment(sketch, "E88.MirrorCS", {"start": v(-33, -74.25) * mm, "end": v(-15, -92.25) * mm});
            skLineSegment(sketch, "E89.MirrorCS", {"start": v(-15, -92.25) * mm, "end": v(-15, -104.25) * mm});
            skArc(sketch, "E90.MirrorCS", {"start": v(15, -104.25) * mm, "mid": v(0, -119.25) * mm, "end": v(-15, -104.25) * mm});
            skLineSegment(sketch, "E91.MirrorCS", {"start": v(15, -92.25) * mm, "end": v(15, -104.25) * mm});
            skLineSegment(sketch, "E92.MirrorCS", {"start": v(15, -92.25) * mm, "end": v(33, -74.25) * mm});
            skCircle(sketch, "E93.MirrorC", {"center": v(0, -104.25) * mm, "radius": 6 * mm});
            skLineSegment(sketch, "E94.0", {"start": v(-90, -64.25) * mm, "end": v(-90, 64.25) * mm});
            skLineSegment(sketch, "E94.2", {"start": v(90, -64.25) * mm, "end": v(90, 64.25) * mm});
            skLineSegment(sketch, "E94.3", {"start": v(-80, -74.25) * mm, "end": v(80, -74.25) * mm});
            skArc(sketch, "E94.4", {"start": v(-90, -64.25) * mm, "mid": v(-87.07, -71.32) * mm, "end": v(-80, -74.25) * mm});
            skArc(sketch, "E94.5", {"start": v(80, -74.25) * mm, "mid": v(87.07, -71.32) * mm, "end": v(90, -64.25) * mm});
            skCircle(sketch, "E94.6", {"center": v(60, -49.5) * mm, "radius": 4 * mm});
            skCircle(sketch, "E94.7", {"center": v(-60, -49.5) * mm, "radius": 4 * mm});
            skCircle(sketch, "E94.8", {"center": v(60, 49.5) * mm, "radius": 4 * mm});
            skCircle(sketch, "E94.9", {"center": v(-60, 49.5) * mm, "radius": 4 * mm});
            skLineSegment(sketch, "E94.10", {"start": v(-60, 36.3) * mm, "end": v(-60, -36.3) * mm});
            skLineSegment(sketch, "E94.11", {"start": v(60, 36.3) * mm, "end": v(60, -36.3) * mm});
            skArc(sketch, "E94.12", {"start": v(-51.27, -46.22) * mm, "mid": v(0, -49.5) * mm, "end": v(51.27, -46.22) * mm});
            skArc(sketch, "E94.13", {"start": v(-60, -36.3) * mm, "mid": v(-57.5, -42.9) * mm, "end": v(-51.27, -46.22) * mm});
            skArc(sketch, "E94.14", {"start": v(51.27, -46.22) * mm, "mid": v(57.5, -42.9) * mm, "end": v(60, -36.3) * mm});
            skArc(sketch, "E94.15", {"start": v(60, 36.3) * mm, "mid": v(57.5, 42.9) * mm, "end": v(51.27, 46.22) * mm});
            skArc(sketch, "E94.16", {"start": v(51.27, 46.22) * mm, "mid": v(0, 49.5) * mm, "end": v(-51.27, 46.22) * mm});
            skArc(sketch, "E94.17", {"start": v(90, 64.25) * mm, "mid": v(87.07, 71.32) * mm, "end": v(80, 74.25) * mm});
            skArc(sketch, "E94.18", {"start": v(-80, 74.25) * mm, "mid": v(-87.07, 71.32) * mm, "end": v(-90, 64.25) * mm});
            skArc(sketch, "E94.19", {"start": v(-51.27, 46.22) * mm, "mid": v(-57.5, 42.9) * mm, "end": v(-60, 36.3) * mm});
            skSolve(sketch);
        }
        {
            var Q0;
            Q0 = qSketchRegion(id + "F17", true);
            var Q1;
            Q1=makeQuery(id+"F2.opExtrude","CAP_FACE",FACE,{"disambiguationData":[OSD([sQuery(id+"F0.wireOp",EDGE,"E12"),sQuery(id+"F0.wireOp",EDGE,"E13"),sQuery(id+"F0.wireOp",EDGE,"E14"),sQuery(id+"F0.wireOp",EDGE,"E15"),sQuery(id+"F0.wireOp",EDGE,"E17.filletArc"),sQuery(id+"F0.wireOp",EDGE,"E18.filletArc"),sQuery(id+"F0.wireOp",EDGE,"E19.filletArc"),sQuery(id+"F0.wireOp",EDGE,"E20.filletArc"),sQuery(id+"F0.wireOp",EDGE,"E25.0"),sQuery(id+"F0.wireOp",EDGE,"E25.1"),sQuery(id+"F0.wireOp",EDGE,"E25.2"),sQuery(id+"F0.wireOp",EDGE,"E25.3"),sQuery(id+"F0.wireOp",EDGE,"E25.4"),sQuery(id+"F0.wireOp",EDGE,"E25.5"),sQuery(id+"F0.wireOp",EDGE,"E25.6"),sQuery(id+"F0.wireOp",EDGE,"E25.7")])],"isStart":false});
            extrude(context, id + "F18", {"entities" : qUnion([Q0]), "endBound" : BoundingType.UP_TO_SURFACE, "endBoundEntityFace" : qUnion([Q1]), "depth" : 25 * mm});
        }
    });
